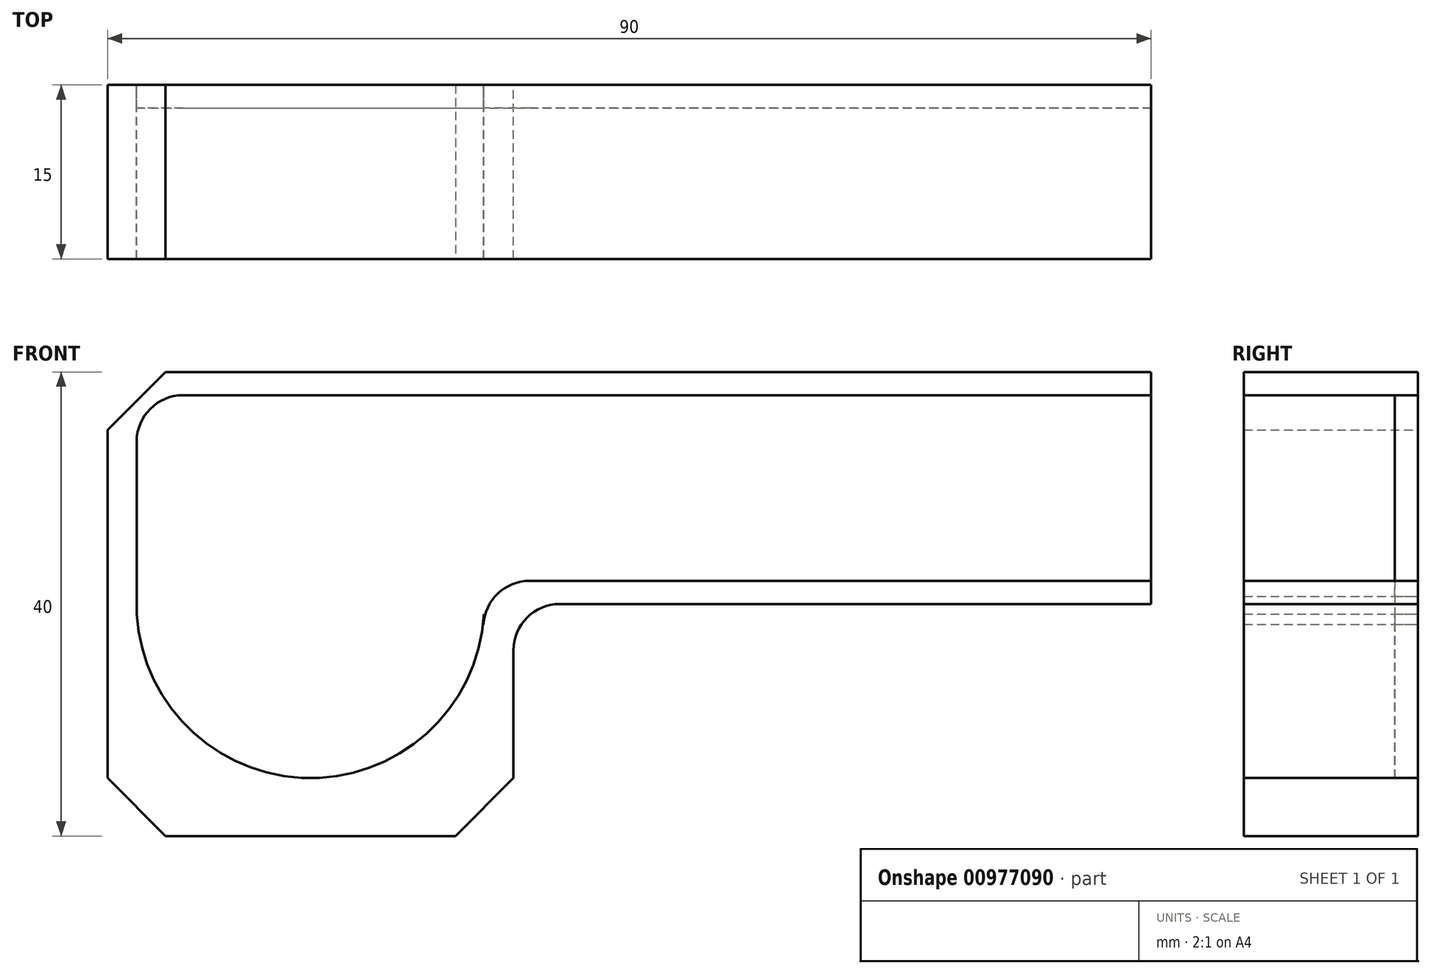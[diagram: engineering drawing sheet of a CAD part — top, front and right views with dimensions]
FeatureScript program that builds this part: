
annotation { "Feature Type Name" : "Feature", "Feature Type Description" : "" }
export const myFeature = defineFeature(function(context is Context, id is Id, definition is map)
    precondition{}
    {
        {
            var Q0;
            Q0=qCreatedBy(makeId("Front.planeOp"),FACE);
            var sketch = newSketch(context, id + "F0", { "sketchPlane" : qUnion([Q0])});
            skLineSegment(sketch, "E0", {"start": v(-50.95, 0) * mm, "end": v(-50.95, 40) * mm});
            skLineSegment(sketch, "E1", {"start": v(-50.95, 40) * mm, "end": v(39.05, 40) * mm});
            skLineSegment(sketch, "E2", {"start": v(39.05, 40) * mm, "end": v(39.05, 20) * mm});
            skLineSegment(sketch, "E3", {"start": v(39.05, 20) * mm, "end": v(-15.95, 20) * mm});
            skLineSegment(sketch, "E4", {"start": v(-15.95, 20) * mm, "end": v(-15.95, 0) * mm});
            skLineSegment(sketch, "E5", {"start": v(-15.95, 0) * mm, "end": v(-50.95, 0) * mm});
            skArc(sketch, "E6", {"start": v(-48.43, 20.67) * mm, "mid": v(-34.22, 5.02) * mm, "end": v(-18.48, 19.12) * mm});
            skPoint(sketch, "E6.centerSnap0", {"position": v(-50.95, 20) * mm});
            skPoint(sketch, "E6.centerSnap1", {"position": v(-33.45, 0) * mm});
            skLineSegment(sketch, "E7", {"start": v(-48.43, 20.67) * mm, "end": v(-48.43, 34) * mm});
            skLineSegment(sketch, "E8", {"start": v(-44.43, 38) * mm, "end": v(39.05, 38) * mm});
            skLineSegment(sketch, "E9", {"start": v(39.05, 38) * mm, "end": v(39.05, 22) * mm});
            skLineSegment(sketch, "E10", {"start": v(39.05, 22) * mm, "end": v(-14.53, 22) * mm});
            skLineSegment(sketch, "E11", {"start": v(-18.48, 19.12) * mm, "end": v(-18.53, 18.23) * mm});
            skPoint(sketch, "E12.visualSharp", {"position": v(-18.3, 22) * mm});
            skArc(sketch, "E12.filletArc", {"start": v(-14.53, 22) * mm, "mid": v(-17.28, 20.9) * mm, "end": v(-18.53, 18.23) * mm});
            skPoint(sketch, "E13.visualSharp", {"position": v(-48.43, 38) * mm});
            skArc(sketch, "E13.filletArc", {"start": v(-44.43, 38) * mm, "mid": v(-47.26, 36.83) * mm, "end": v(-48.43, 34) * mm});
            skSolve(sketch);
        }
        {
            var Q0;
            Q0=makeQuery(id+"F0.imprint","IMPRINT",FACE,{"disambiguationData":[TD([[makeQuery(id+"F0.imprint","IMPRINT",EDGE,{"derivedFrom":sQuery(id+"F0.wireOp",EDGE,"E0")}),-1.0]])]});
            extrude(context, id + "F1", {"entities" : qUnion([Q0]), "depth" : 15 * mm, "offsetDistance" : 25 * mm});
        }
        {
            var Q0;
            Q0=makeQuery(id+"F1.opExtrude","CAP_FACE",FACE,{"disambiguationData":[OSD([sQuery(id+"F0.wireOp",EDGE,"E0"),sQuery(id+"F0.wireOp",EDGE,"E1"),sQuery(id+"F0.wireOp",EDGE,"E2"),sQuery(id+"F0.wireOp",EDGE,"E3"),sQuery(id+"F0.wireOp",EDGE,"E4"),sQuery(id+"F0.wireOp",EDGE,"E5"),sQuery(id+"F0.wireOp",EDGE,"E6"),sQuery(id+"F0.wireOp",EDGE,"E7"),sQuery(id+"F0.wireOp",EDGE,"E8"),sQuery(id+"F0.wireOp",EDGE,"E10"),sQuery(id+"F0.wireOp",EDGE,"E11"),sQuery(id+"F0.wireOp",EDGE,"E12.filletArc"),sQuery(id+"F0.wireOp",EDGE,"E13.filletArc")])],"isStart":true});
            var sketch = newSketch(context, id + "F2", { "sketchPlane" : qUnion([Q0])});
            skLineSegment(sketch, "E14", {"start": v(-39.05, 22) * mm, "end": v(-39.05, 38) * mm});
            skSolve(sketch);
        }
        {
            var Q0;
            Q0=makeQuery(id+"F2.imprint","IMPRINT",FACE,{"disambiguationData":[TD([[makeQuery(id+"F2.imprint","IMPRINT",EDGE,{"derivedFrom":sQuery(id+"F2.wireOp",EDGE,"E14")}),-1.0]])]});
            extrude(context, id + "F3", {"entities" : qUnion([Q0]), "oppositeDirection" : true, "depth" : 2 * mm, "offsetDistance" : 25 * mm});
        }
        {
            var Q0;
            Q0=makeQuery(id+"F1.opExtrude","SWEPT_EDGE",EDGE,{"disambiguationData":[OSD([sQuery(id+"F0.wireOp",EDGE,"E0"),sQuery(id+"F0.wireOp",EDGE,"E5")])]});
            var Q1;
            Q1=makeQuery(id+"F1.opExtrude","SWEPT_EDGE",EDGE,{"disambiguationData":[OSD([sQuery(id+"F0.wireOp",EDGE,"E4"),sQuery(id+"F0.wireOp",EDGE,"E5")])]});
            var Q2;
            Q2=makeQuery(id+"F1.opExtrude","SWEPT_EDGE",EDGE,{"disambiguationData":[OSD([sQuery(id+"F0.wireOp",EDGE,"E0"),sQuery(id+"F0.wireOp",EDGE,"E1")])]});
            chamfer(context, id + "F4", {"entities" : qUnion([Q0, Q1, Q2]), "width" : 5 * mm, "tangentPropagation" : true});
        }
        {
            var Q0;
            Q0=makeQuery(id+"F1.opExtrude","SWEPT_EDGE",EDGE,{"disambiguationData":[OSD([sQuery(id+"F0.wireOp",EDGE,"E3"),sQuery(id+"F0.wireOp",EDGE,"E4")])]});
            fillet(context, id + "F5", {"entities" : qUnion([Q0]), "radius" : 4 * mm, "tangentPropagation" : true, "allowEdgeOverflow" : false});
        }
    });
